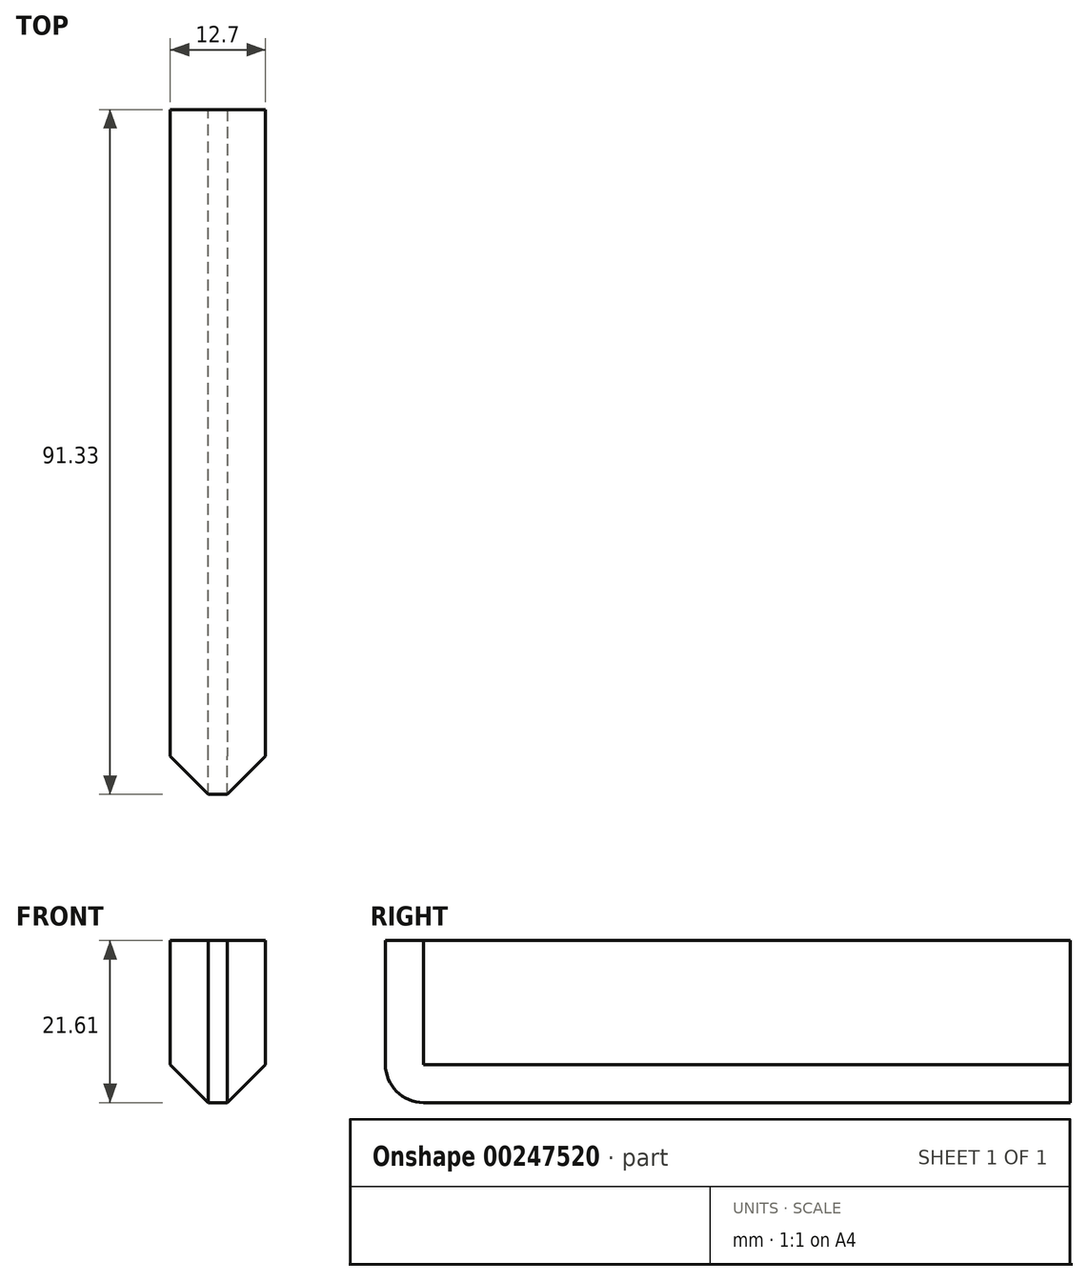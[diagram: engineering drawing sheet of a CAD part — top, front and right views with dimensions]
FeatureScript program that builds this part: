
annotation { "Feature Type Name" : "Feature", "Feature Type Description" : "" }
export const myFeature = defineFeature(function(context is Context, id is Id, definition is map)
    precondition{}
    {
        {
            var Q0;
            Q0=qCreatedBy(makeId("Right.planeOp"),FACE);
            var sketch = newSketch(context, id + "F0", { "sketchPlane" : qUnion([Q0])});
            skLineSegment(sketch, "E0.bottom", {"start": v(-48.62, 33.44) * mm, "end": v(42.7, 33.44) * mm});
            skLineSegment(sketch, "E0.top", {"start": v(-48.62, 11.83) * mm, "end": v(42.7, 11.83) * mm});
            skLineSegment(sketch, "E0.left", {"start": v(-48.62, 33.44) * mm, "end": v(-48.62, 11.83) * mm});
            skLineSegment(sketch, "E0.right", {"start": v(42.7, 33.44) * mm, "end": v(42.7, 11.83) * mm});
            skSolve(sketch);
        }
        {
            var Q0;
            Q0 = qSketchRegion(id + "F0", true);
            extrude(context, id + "F1", {"entities" : qUnion([Q0]), "depth" : 12.7 * mm});
        }
        {
            var Q0;
            Q0=makeQuery(id+"F1.opExtrude","SWEPT_EDGE",EDGE,{"disambiguationData":[OSD([sQuery(id+"F0.wireOp",EDGE,"E0.top"),sQuery(id+"F0.wireOp",EDGE,"E0.left")])]});
            fillet(context, id + "F2", {"entities" : qUnion([Q0]), "radius" : 5.08 * mm, "tangentPropagation" : true, "allowEdgeOverflow" : false});
        }
        {
            var Q0;
            Q0=makeQuery(id+"F1.opExtrude","CAP_EDGE",EDGE,{"disambiguationData":[OSD([sQuery(id+"F0.wireOp",EDGE,"E0.top")])],"isStart":false});
            var Q1;
            Q1=makeQuery(id+"F1.opExtrude","CAP_EDGE",EDGE,{"disambiguationData":[OSD([sQuery(id+"F0.wireOp",EDGE,"E0.top")])],"isStart":true});
            var Q2;
            Q2=makeQuery(id+"F1.opExtrude","CAP_EDGE",EDGE,{"disambiguationData":[OSD([sQuery(id+"F0.wireOp",EDGE,"E0.left")])],"isStart":true});
            chamfer(context, id + "F3", {"entities" : qUnion([Q0, Q1, Q2]), "width" : 5.08 * mm, "tangentPropagation" : true});
        }
    });
